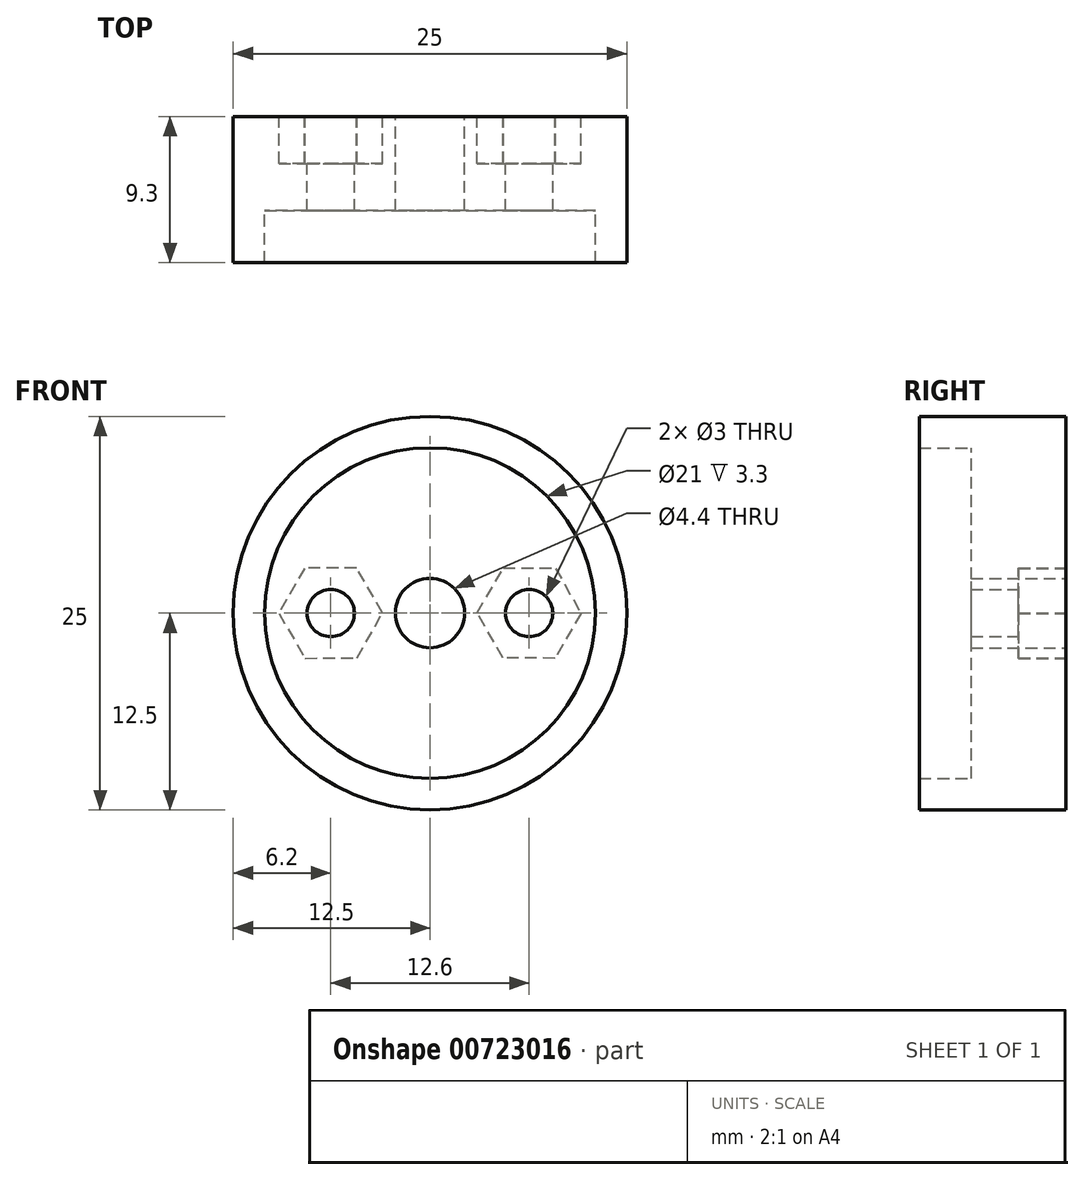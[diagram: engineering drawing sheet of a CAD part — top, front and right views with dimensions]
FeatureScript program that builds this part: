
annotation { "Feature Type Name" : "Feature", "Feature Type Description" : "" }
export const myFeature = defineFeature(function(context is Context, id is Id, definition is map)
    precondition{}
    {
        {
            var Q0;
            Q0=qCreatedBy(makeId("Front.planeOp"),FACE);
            var sketch = newSketch(context, id + "F0", { "sketchPlane" : qUnion([Q0])});
            skCircle(sketch, "E0", {"center": v(0, 0) * mm, "radius": 2.2 * mm});
            skCircle(sketch, "E1", {"center": v(0, 0) * mm, "radius": 10.5 * mm});
            skCircle(sketch, "E2", {"center": v(0, 0) * mm, "radius": 12.5 * mm});
            skCircle(sketch, "E3", {"center": v(6.3, 0) * mm, "radius": 1.5 * mm});
            skCircle(sketch, "E4.MirrorC", {"center": v(-6.3, 0) * mm, "radius": 1.5 * mm});
            skSolve(sketch);
        }
        {
            var Q0;
            Q0=makeQuery(id+"F0.imprint","IMPRINT",FACE,{"disambiguationData":[TD([[makeQuery(id+"F0.imprint","IMPRINT",EDGE,{"derivedFrom":sQuery(id+"F0.wireOp",EDGE,"E1")}),-1.0]])]});
            extrude(context, id + "F1", {"entities" : qUnion([Q0]), "depth" : 9.3 * mm, "offsetDistance" : 25 * mm});
        }
        {
            var Q0;
            Q0=makeQuery(id+"F0.imprint","IMPRINT",FACE,{"disambiguationData":[TD([[makeQuery(id+"F0.imprint","IMPRINT",EDGE,{"derivedFrom":sQuery(id+"F0.wireOp",EDGE,"E0")}),-1.0]])]});
            extrude(context, id + "F2", {"entities" : qUnion([Q0]), "operationType" : NewBodyOperationType.ADD, "depth" : 6 * mm, "offsetDistance" : 25 * mm});
        }
        {
            var Q0;
            {var subQ0=sQuery(id+"F0.wireOp",EDGE,"E1");Q0=makeQuery(id+"F2.boolean.opBoolean","MERGE",FACE,{"derivedFrom":[makeQuery(id+"F1.opExtrude","CAP_FACE",FACE,{"disambiguationData":[OSD([subQ0,sQuery(id+"F0.wireOp",EDGE,"E2")])],"isStart":true}),makeQuery(id+"F2.opExtrude","CAP_FACE",FACE,{"disambiguationData":[OSD([sQuery(id+"F0.wireOp",EDGE,"E0"),subQ0,sQuery(id+"F0.wireOp",EDGE,"E3"),sQuery(id+"F0.wireOp",EDGE,"E4.MirrorC")])],"isStart":true})]});}
            var sketch = newSketch(context, id + "F3", { "sketchPlane" : qUnion([Q0])});
            skLineSegment(sketch, "E5.0", {"start": v(9.6, -0.02) * mm, "end": v(7.93, -2.87) * mm});
            skLineSegment(sketch, "E5.1", {"start": v(7.93, -2.87) * mm, "end": v(4.63, -2.85) * mm});
            skLineSegment(sketch, "E5.2", {"start": v(4.63, -2.85) * mm, "end": v(3, 0.02) * mm});
            skLineSegment(sketch, "E5.3", {"start": v(3, 0.02) * mm, "end": v(4.67, 2.87) * mm});
            skLineSegment(sketch, "E5.4", {"start": v(4.67, 2.87) * mm, "end": v(7.97, 2.85) * mm});
            skLineSegment(sketch, "E5.5", {"start": v(7.97, 2.85) * mm, "end": v(9.6, -0.02) * mm});
            skPoint(sketch, "E5.0.midPoint", {"position": v(8.77, -1.44) * mm});
            skLineSegment(sketch, "E6.MirrorCS", {"start": v(-3, 0.02) * mm, "end": v(-4.67, 2.87) * mm});
            skLineSegment(sketch, "E7.MirrorCS", {"start": v(-4.67, 2.87) * mm, "end": v(-7.97, 2.85) * mm});
            skLineSegment(sketch, "E8.MirrorCS", {"start": v(-7.97, 2.85) * mm, "end": v(-9.6, -0.02) * mm});
            skLineSegment(sketch, "E9.MirrorCS", {"start": v(-9.6, -0.02) * mm, "end": v(-7.93, -2.87) * mm});
            skLineSegment(sketch, "E10.MirrorCS", {"start": v(-7.93, -2.87) * mm, "end": v(-4.63, -2.85) * mm});
            skLineSegment(sketch, "E11.MirrorCS", {"start": v(-4.63, -2.85) * mm, "end": v(-3, 0.02) * mm});
            skSolve(sketch);
        }
        {
            var Q0;
            Q0=makeQuery(id+"F3.imprint","IMPRINT",FACE,{"disambiguationData":[TD([[makeQuery(id+"F3.imprint","IMPRINT",EDGE,{"derivedFrom":sQuery(id+"F3.wireOp",EDGE,"E6.MirrorCS")}),1.0]])]});
            var Q1;
            Q1=makeQuery(id+"F3.imprint","IMPRINT",FACE,{"disambiguationData":[TD([[makeQuery(id+"F3.imprint","IMPRINT",EDGE,{"derivedFrom":sQuery(id+"F3.wireOp",EDGE,"E5.0")}),-1.0]])]});
            extrude(context, id + "F4", {"entities" : qUnion([Q0, Q1]), "operationType" : NewBodyOperationType.REMOVE, "oppositeDirection" : true, "depth" : 3 * mm, "offsetDistance" : 25 * mm});
        }
    });
